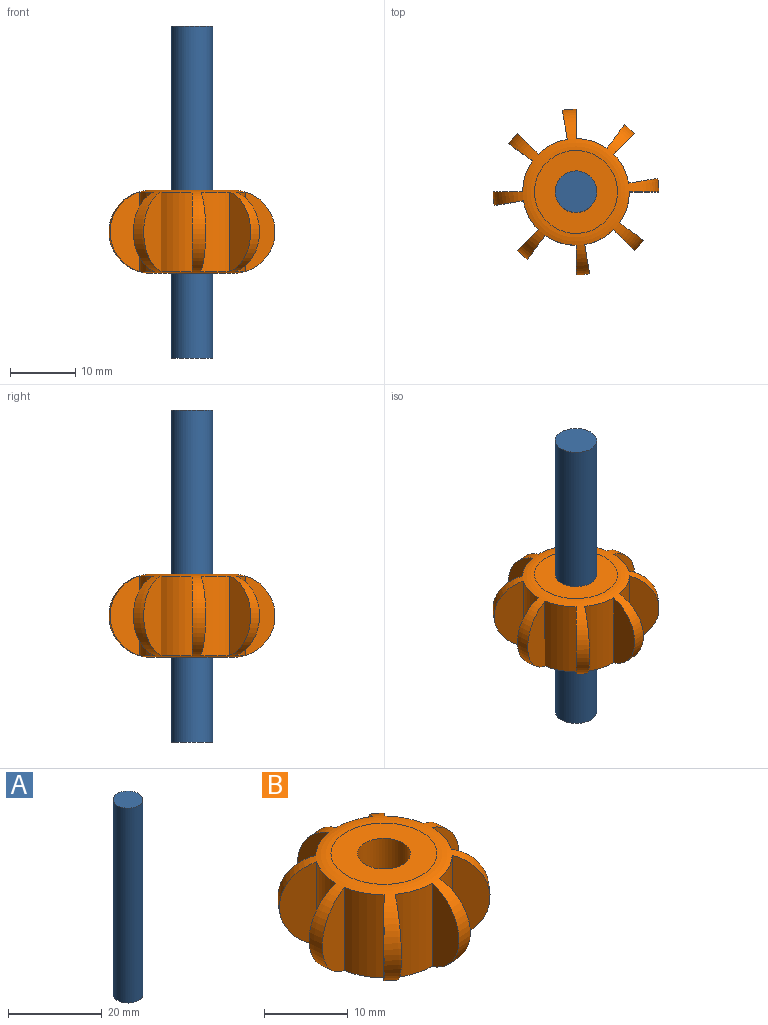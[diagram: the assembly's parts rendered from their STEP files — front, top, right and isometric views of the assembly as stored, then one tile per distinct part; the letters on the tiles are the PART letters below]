
ASSEMBLY  parts=2 mates=1
PART A: 3 faces, bbox 6.4x6.4x50.8 mm
  f0: cylinder r=3.17mm len=50.8mm, axis (0,0,-1), area 1013.4mm2, adj f1,f2
  f1: plane 6.35x6.35mm, normal (0,0,1), area 31.7mm2, adj f0
  f2: plane 6.35x6.35mm, normal (0,0,-1), area 31.7mm2, adj f0
PART B: 28 faces, bbox 27.5x27.5x12.7 mm
  f0: plane 12.17x3.21mm, normal (0.71,-0.71,0), area 40.6mm2, adj f1,f21
  f1: cylinder r=8.16mm len=12.17mm, axis (0,0,-1), area 61.7mm2, adj f0,f2,f21
  f2: plane 12.17x4.48mm, normal (-0.16,0.99,0), area 40.6mm2, adj f1,f21
  f3: plane 12.17x4.54mm, normal (0,-1,0), area 40.6mm2, adj f4,f21
  f4: cylinder r=8.16mm len=12.17mm, axis (0,0,-1), area 61.7mm2, adj f3,f5,f21
  f5: plane 12.17x3.69mm, normal (0.58,0.81,0), area 40.6mm2, adj f4,f21
  f6: plane 12.17x3.21mm, normal (-0.71,-0.71,0), area 40.6mm2, adj f7,f21
  f7: cylinder r=8.16mm len=12.17mm, axis (0,0,-1), area 61.7mm2, adj f6,f8,f21
  f8: plane 12.17x4.48mm, normal (0.99,0.16,0), area 40.6mm2, adj f7,f21
  f9: plane 12.17x4.54mm, normal (-1,0,0), area 40.6mm2, adj f10,f21
  f10: cylinder r=8.16mm len=12.17mm, axis (0,0,-1), area 61.7mm2, adj f9,f11,f21
  f11: plane 12.17x3.69mm, normal (0.81,-0.58,0), area 40.6mm2, adj f10,f21
  f12: plane 12.17x3.21mm, normal (-0.71,0.71,0), area 40.6mm2, adj f13,f21
  f13: cylinder r=8.16mm len=12.17mm, axis (0,0,-1), area 61.7mm2, adj f12,f14,f21
  f14: plane 12.17x4.48mm, normal (0.16,-0.99,0), area 40.6mm2, adj f13,f21
  f15: plane 12.17x4.54mm, normal (0,1,0), area 40.6mm2, adj f16,f21
  f16: cylinder r=8.16mm len=12.17mm, axis (0,0,-1), area 61.7mm2, adj f15,f17,f21
  f17: plane 12.17x3.69mm, normal (-0.58,-0.81,0), area 40.6mm2, adj f16,f21
  f18: plane 12.17x3.21mm, normal (0.71,0.71,0), area 40.6mm2, adj f19,f21
  f19: cylinder r=8.16mm len=12.17mm, axis (0,0,-1), area 61.7mm2, adj f18,f20,f21
  f20: plane 12.17x4.48mm, normal (-0.99,-0.16,0), area 40.6mm2, adj f19,f21
  f21: torus R=6.35mm, axis (0,0,1), area 405.8mm2, adj f0,f1,f2,f3,f4,f5,f6,f7
  f22: plane 12.7x12.7mm, normal (0,0,1), area 95mm2, adj f21,f27
  f23: plane 12.7x12.7mm, normal (0,0,-1), area 95mm2, adj f21,f27
  f24: plane 12.17x4.54mm, normal (1,0,0), area 40.6mm2, adj f21,f25
  f25: cylinder r=8.16mm len=12.17mm, axis (0,0,-1), area 61.7mm2, adj f21,f24,f26
  f26: plane 12.17x3.69mm, normal (-0.81,0.58,0), area 40.6mm2, adj f21,f25
  f27: cylinder r=3.17mm len=12.7mm, axis (0,0,-1), area 253.4mm2, adj f22,f23
PLACE A at identity
PLACE B t=(0,0,-12.44)mm
MATE cylindrical B.f7 <-> A.f0  axis (0,0,-1) through (0,0,0)mm
